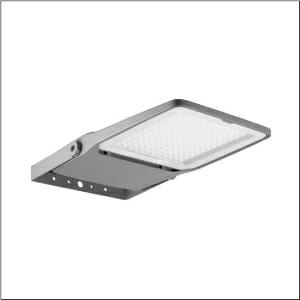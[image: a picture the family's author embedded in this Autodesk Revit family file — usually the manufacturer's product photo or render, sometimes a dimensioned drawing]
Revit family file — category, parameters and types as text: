
# Revit family: floodlight_fl_20_midi___rs17_5xa7682e2b2ac_f397
name_source: partatom
category: Lighting Fixtures
units: mm (PartAtom-declared; Revit-internal decimal feet)

## family parameters
Cut with Voids When Loaded = No
Host = Face
Light Source = No
Part Type = Normal
Room Calculation Point = No
Round Connector Dimension = Use Diameter
Shared = No

## types (1)
- --- (1 x LED 4000K / CRI = 70 (unbekannt), 29150 lm, 4000K)
    Apparent Load = 208 VA
    CIE Flux Codes = 79 92 99 100 100
    Color Rendering = 70
    Color Temperature = 4000K
    Default Elevation = 1800 mm
    Description = Floodlight FL 20 midi, floodlight, primary light control with lens, of plastic, primary optical cover: protective disc, of toughened safety glass, transparent, light distribution: RS17, light emission: direct distribution, primary light characteristic: rotationally symmetric, installation type: surface-mounted, LED, High Power LED, rated luminous flux: 29.150lm, luminous efficacy: 140lm/W, light colour: 740, colour temperature: 4000K, control gear: ECG Plus, control: flexible luminous flux parameterisation, time-dependent luminous flux control, digital communication interface, power reduction, overheat protection, electronic power reduction, with terminal, 5-pole, max. 2.5mm², mains connection: 220..240V, AC, 50/60Hz, rated input power: 208W, LED unit, of diecast aluminium, powder-coated, Siteco® metallic grey (DB 702S), corrosivity category C5 mid according to DIN EN ISO 12944, incl. 1x M20 cable gland for cable Ø 6.5..12mm, length: 731mm, width: 450mm, height: 76mm, housing frame, of diecast aluminium, powder-coated, Siteco® metallic grey (DB 702S), wall fastening, of steel, powder-coated, Siteco® metallic grey (DB 702S), DALI, protection rating (complete): IP66, insulation class (complete): insulation class II (safety insulation), certification: CE, ENEC, VDE, protection symbol: D, permissible operating ambient temperature: -40..+40°C, permissible operating ambient temperature for outdoor applications: -40..+50°C, standard: DIN EN 12944, packaging unit: 1 piece

Light Distribution: RS17
    Height = 76 mm
    Lamp = 1 x LED 4000K / CRI >= 70 (unbekannt)
    Lamp Light Flux = 29150 lm
    Lamp count = 1
    Length = 731 mm
    Luminous efficacy = 140 lm/W
    Manufacturer = Siteco
    ModVariant = No
    Model = 5XA7682E2B2AC
    Mounting Place = Wall
    Mounting Type = Surface mounted
    Number of Poles = 1
    OnlyDefault = Yes
    Power Factor = 1
    Product Name = Floodlight FL 20 midi | RS17
    Product group = floodlight | wall mounted
    ProductGroupID = 2001
    Protection Class = Protection class II
    Protection Degree = IP 66
    RLX_Detail_Level = 1
    RLX_Emergency_Light_Flux = 0 lm
    RLX_Emergency_Type = 0
    RLX_Emergency_Type_DB = No
    RlxData = <blob elided: 86593 chars, md5=67617c1a>
    Socket = socket
    Standby Power = 0 W
    System Light Flux = 29150 lm
    System Power = 208 W
    Type Comments = factory setting: luminous flux: 100 % | dim-lin: 254 | 484 mA
    Type Image = l_1005944.jpg
    URL = http://relux.com
    VarID = @adj_146413
    Voltage = 0 V
    Weight = 0.00 kg
    Width = 450 mm

## geometry (parser evidence)
native form markers: Blend x4, Sweep x13
no freeform markers — native parametric forms only
